# Revit family: RN 55041 Optipress-Therm-Vis de rappel
name_source: partatom
category: Rohrformteile
units: mm (PartAtom-declared; Revit-internal decimal feet)

## family parameters
Arbeitsebenenbasiert = Nein
Beim Laden mit Abzugskörper schneiden = Nein
Bemaßung runder Anschluss = Durchmesser verwenden
Gemeinsam genutzt = Nein
Immer vertikal = Ja
Teiletyp = Verbindung

## types (7) — shared parameters
1.010.00.2 Blattnummer der Richtlinie = 29
1.010.00.3 Ausgabedatum (Monat) der Richtlinie = 201308
1.010.00.4 Herstellername = R. Nussbaum AG
1.010.00.5 Revisionsdatum der Datei = 20190521
1.010.00.6 Webadresse des Herstellers = http://www.nussbaum.ch
1.100.00.4 Produktbezeichnung = Versorgung
1.110.00.2 Index = 1
1.110.00.4 Produktbezeichnung = Optipress-Therm
1.960/3L.00.8 Link (URL) = https://www.nussbaum.ch
29.700.00.4 Produktname = Optipress-Therm-Verschraubung
29.700.00.5 Produktkennung = 2
29.700.00.6 Querschnittsform = 1
29.700.00.7 Nennweitensystem = DN
29.700.00.8 Nenndrucksystem = PN
29.710.02.4 Nenndruck = 16
29.710.02.5 max. zul. Überdruck [hPa] = 1600
29.710.02.7 max. zul. Dauer-Betriebsdruck [hPa] = 1600
29.710.02.9 max. zul. Dauer-Betriebstemperatur [°C] = 95
Connector Visibility = Nein
EnclosingSpace Visibility = Nein
Hersteller = R. Nussbaum AG

## per-type parameters (varying)
| type | 1.800.00.3 TGA-Nummer | 1.800.00.4 Kommentarfeld | 1.810.00.3 Hersteller-Bestellnummer | 1.810.00.4 DATANORM-Nummer | 1.810.00.5 StLB-Nummer | 1.810.00.6 GTIN-Nummer | 29.710.02.10 Formstück-Gewicht [kg] | 29.710.02.3 Benennung | CONNECTOR0_DIAMETER_dX_0r | CONNECTOR0_dX_01 | CONNECTOR0_ref_dX | CONNECTOR1_DIAMETER_dX_0r | CONNECTOR1_dX_00 | CONNECTOR1_dX_01 | CONNECTOR1_ref_dX | Modell | R. Nussbaum AG 55041.22 de Visibility | R. Nussbaum AG 55041.23 de Visibility | R. Nussbaum AG 55041.24 de Visibility | R. Nussbaum AG 55041.25 de Visibility | R. Nussbaum AG 55041.26 de Visibility | R. Nussbaum AG 55041.27 de Visibility | R. Nussbaum AG 55041.28 de Visibility | Typenkommentare |
| DN=50 | 01900100000000000000000000000000000000000000000024000000000000000007 | 55041.28, Optipress-Therm-Verschraubung, DN=50, L=133 | 55041.28 | 55041.28 | 256.168 | 7612945663191 | 1.124 | Optipress-Therm-Verschraubung, DN=50, L=133 | 50 mm | 40 mm | 40 mm | 50 mm | 93 mm  [stored 0.305118 ft] | 133 mm | 93 mm  [stored 0.305118 ft] | 55041.28 | Nein | Nein | Nein | Nein | Nein | Nein | Ja | Optipress-Therm-Vis de rappel DN=50 |
| DN=40 | 01900100000000000000000000000000000000000000000024000000000000000006 | 55041.27, Optipress-Therm-Verschraubung, DN=40, L=115 | 55041.27 | 55041.27 | 256.157 | 7612945663184 | 0.611 | Optipress-Therm-Verschraubung, DN=40, L=115 | 40 mm | 36 mm | 36 mm | 40 mm | 79 mm | 115 mm | 79 mm | 55041.27 | Nein | Nein | Nein | Nein | Nein | Ja | Nein | Optipress-Therm-Vis de rappel DN=40 |
| DN=32 | 01900100000000000000000000000000000000000000000024000000000000000005 | 55041.26, Optipress-Therm-Verschraubung, DN=32, L=95 | 55041.26 | 55041.26 | 256.146 | 7612945663177 | 0.444 | Optipress-Therm-Verschraubung, DN=32, L=95 | 32 mm | 26 mm | 26 mm | 32 mm | 69 mm | 95 mm | 69 mm | 55041.26 | Nein | Nein | Nein | Nein | Ja | Nein | Nein | Optipress-Therm-Vis de rappel DN=32 |
| DN=25 | 01900100000000000000000000000000000000000000000024000000000000000004 | 55041.25, Optipress-Therm-Verschraubung, DN=25, L=91 | 55041.25 | 55041.25 | 256.135 | 7612945663160 | 0.377 | Optipress-Therm-Verschraubung, DN=25, L=91 | 25 mm  [stored 0.082021 ft] | 24 mm | 24 mm | 25 mm  [stored 0.082021 ft] | 67 mm | 91 mm | 67 mm | 55041.25 | Nein | Nein | Nein | Ja | Nein | Nein | Nein | Optipress-Therm-Vis de rappel DN=25 |
| DN=20 | 01900100000000000000000000000000000000000000000024000000000000000003 | 55041.24, Optipress-Therm-Verschraubung, DN=20, L=84 | 55041.24 | 55041.24 | 256.124 | 7612945663153 | 0.228 | Optipress-Therm-Verschraubung, DN=20, L=84 | 20 mm | 24 mm | 24 mm | 20 mm | 60 mm | 84 mm | 60 mm | 55041.24 | Nein | Nein | Ja | Nein | Nein | Nein | Nein | Optipress-Therm-Vis de rappel DN=20 |
| DN=15 | 01900100000000000000000000000000000000000000000024000000000000000002 | 55041.23, Optipress-Therm-Verschraubung, DN=15, L=79 | 55041.23 | 55041.23 | 256.113 | 7612945663146 | 0.14 | Optipress-Therm-Verschraubung, DN=15, L=79 | 15 mm  [stored 0.0492126 ft] | 22 mm | 22 mm | 15 mm  [stored 0.0492126 ft] | 57 mm | 79 mm | 57 mm | 55041.23 | Nein | Ja | Nein | Nein | Nein | Nein | Nein | Optipress-Therm-Vis de rappel DN=15 |
| DN=12 | 01900100000000000000000000000000000000000000000024000000000000000001 | 55041.22, Optipress-Therm-Verschraubung, DN=12, L=77 | 55041.22 | 55041.22 | 256.112 | 7612945663139 | 0.136 | Optipress-Therm-Verschraubung, DN=12, L=77 | 12 mm  [stored 0.0393701 ft] | 22 mm | 22 mm | 12 mm  [stored 0.0393701 ft] | 55 mm  [stored 0.180446 ft] | 77 mm  [stored 0.252625 ft] | 55 mm  [stored 0.180446 ft] | 55041.22 | Ja | Nein | Nein | Nein | Nein | Nein | Nein | Optipress-Therm-Vis de rappel DN=12 |

note: [stored X ft] marks values corroborated as IEEE doubles in the binary element streams (Revit-internal decimal feet)

## geometry (parser evidence)
native form markers: Sweep x1
no freeform markers — native parametric forms only
